# Revit family: HERZ Strömax клапан балансировочный с измерительными клапанами 4217 GML
name_source: partatom
category: Rohrzubehör
units: mm (PartAtom-declared; Revit-internal decimal feet)

## family parameters
Arbeitsebenenbasiert = Nein
Beim Laden mit Abzugskörper schneiden = Nein
Bemaßung runder Anschluss = Durchmesser verwenden
Gemeinsam genutzt = Nein
Immer vertikal = Ja
OmniClass-Nummer = 23.65.55.14
OmniClass-Titel = Valves for Liquid Services
Teiletyp = Unterbricht

## types (1)
- HERZ Strömax клапан балансировочный с измерительными клапанами 4217 GML
    D04 = 9 mm  [stored 0.0295276 ft]
    H03 = 10 mm  [stored 0.0328084 ft]
    Hersteller = HERZ Armaturen Ges.m.b.H.
    MD01 = 9.5 mm  [stored 0.031168 ft]
    S02 = 60 mm  [stored 0.19685 ft]
    SCRNCODE = 05;07;02
    SCRNSEQ = ARM;ARM_TYP="STRV";2
    SC_NennweiteBerechnet = 0
    URL = www.herz-armaturen.ru
    Vorgabe-Ansicht = 0 mm  [stored 0 ft]
    W01 = 30.00°
    W02 = 60.00°
    Измерение перепада давления = Клапаны STRÖMAX-GML оснащен двумя измерительными клапанами:
с помощью измерительного прибора можно измерить перепад давления и по нему определить текущий расход в зависимости от степени преднастройки.
HERZ Измерительный компьютер (1 8900 05) позволяет напрямую считывать расход (см. руководство к измерительным приборам).
    Исполнение = STRÖMAX-GML Балансировочный клапан с измерительными клапанами и подключением импульсной трубки, 1/2′′ – 3′′.
Исполнение с прямым невыдвижным шпинделем, муфта х муфта, латунный корпус без покрытия, уплотнение шпинделя двойным кольцевым уплотнением O-Ring, преднастройка посредством ограничения хода внутреннего шпинделя, цифровые показания степени настройки отображаются в окне маховика.
Один измерительный клапан расположен перед седлом балансировочного клапана, другой измерительный клапан с возможностью подключения импульсной трубки - после седла.
    Корпус = латунь, устойчивая к селективной цинковой коррозии
    Макс. рабочая температура (до DN32) = 130 °C
    Макс. рабочая температура (с DN40) = 110 °C
    Макс. рабочее давление = 1600000.0 Pa
    Область применения = Балансировочные клапаны применяются для гидравлической балансировки систем отопления и охлаждения, регулировки магистральных трубопроводов, стояков, теплообменников, регистров отопления и охлаждения.
    Положение клапана при монтаже = Неподнимающийся шпиндель, расположенный перпендикулярно оси клапана, обеспечивает доступность и лёгкость в обслуживании в любом монтажном положении.
    Среда = Качество теплоносителя в соответствии с ÖNORM H5195 и VDI 2035.
Допускается использование этилен- и пропиленгликоля в соотношении 25-50% с водой.

note: [stored X ft] marks values corroborated as IEEE doubles in the binary element streams (Revit-internal decimal feet)
